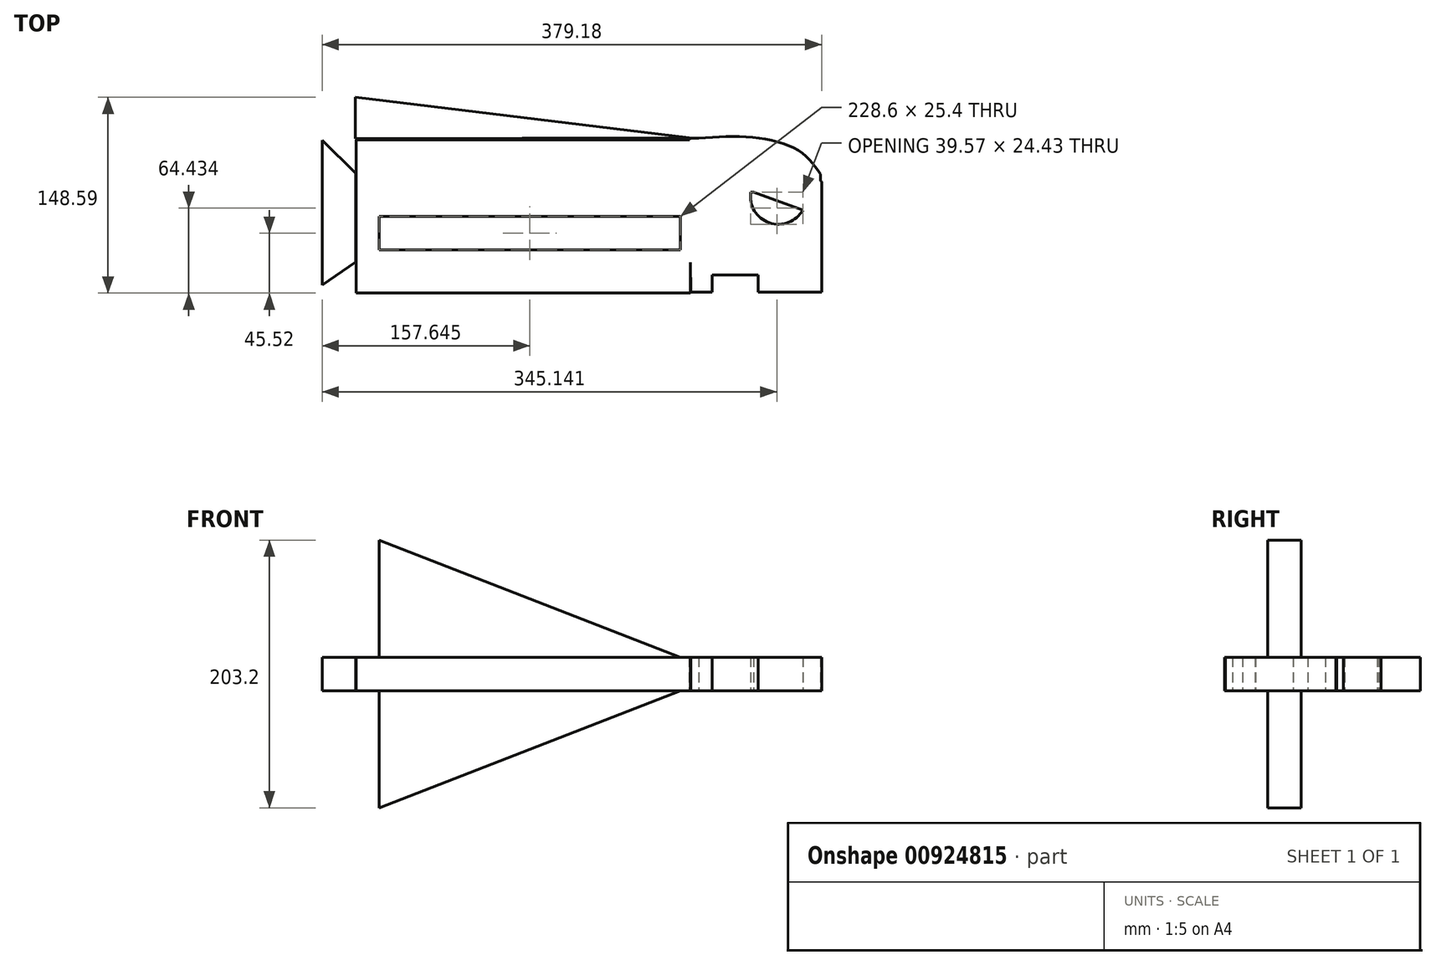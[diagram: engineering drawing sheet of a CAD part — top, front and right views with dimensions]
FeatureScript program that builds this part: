
annotation { "Feature Type Name" : "Feature", "Feature Type Description" : "" }
export const myFeature = defineFeature(function(context is Context, id is Id, definition is map)
    precondition{}
    {
        {
            var Q0;
            Q0=qCreatedBy(makeId("Top.planeOp"),FACE);
            var sketch = newSketch(context, id + "F0", { "sketchPlane" : qUnion([Q0])});
            skLineSegment(sketch, "E0.bottom", {"start": v(126.83, 58.22) * mm, "end": v(-126.83, 58.22) * mm});
            skLineSegment(sketch, "E0.top", {"start": v(126.83, -58.22) * mm, "end": v(-126.83, -58.22) * mm});
            skLineSegment(sketch, "E0.left", {"start": v(126.83, 58.22) * mm, "end": v(126.83, -58.22) * mm});
            skLineSegment(sketch, "E0.right", {"start": v(-126.83, 58.22) * mm, "end": v(-126.83, -58.22) * mm});
            skPoint(sketch, "E0.middle", {"position": v(0, 0) * mm});
            skSolve(sketch);
        }
        {
            var Q0;
            Q0=qCreatedBy(makeId("Top.planeOp"),FACE);
            var sketch = newSketch(context, id + "F1", { "sketchPlane" : qUnion([Q0])});
            skLineSegment(sketch, "E1", {"start": v(126.1, 59.34) * mm, "end": v(175.56, 59.34) * mm});
            skLineSegment(sketch, "E2", {"start": v(175.56, 59.34) * mm, "end": v(175.56, 41.8) * mm});
            skLineSegment(sketch, "E3", {"start": v(175.56, 41.8) * mm, "end": v(207.48, 41.8) * mm});
            skLineSegment(sketch, "E4", {"start": v(207.48, 41.8) * mm, "end": v(226.37, 26.23) * mm});
            skLineSegment(sketch, "E5", {"start": v(226.37, 26.23) * mm, "end": v(226.37, 0) * mm});
            skLineSegment(sketch, "E6", {"start": v(226.37, 0) * mm, "end": v(226.37, -17.54) * mm});
            skLineSegment(sketch, "E7", {"start": v(226.37, -17.54) * mm, "end": v(226.37, -44.52) * mm});
            skLineSegment(sketch, "E8", {"start": v(226.37, -44.52) * mm, "end": v(226.37, -57.55) * mm});
            skLineSegment(sketch, "E9", {"start": v(226.37, -57.55) * mm, "end": v(178.26, -57.55) * mm});
            skLineSegment(sketch, "E10", {"start": v(178.26, -57.55) * mm, "end": v(178.26, -44.52) * mm});
            skLineSegment(sketch, "E11", {"start": v(178.26, -44.52) * mm, "end": v(143.2, -44.52) * mm});
            skLineSegment(sketch, "E12", {"start": v(143.2, -44.52) * mm, "end": v(143.2, -57.55) * mm});
            skLineSegment(sketch, "E13", {"start": v(143.2, -57.55) * mm, "end": v(127, -57.55) * mm});
            skLineSegment(sketch, "E14", {"start": v(127, -57.55) * mm, "end": v(126.1, 59.34) * mm});
            skCircle(sketch, "E15", {"center": v(193.58, 15.27) * mm, "radius": 21.27 * mm});
            skPoint(sketch, "E15.first.point", {"position": v(180.96, 32.38) * mm});
            skPoint(sketch, "E15.second.point", {"position": v(208.39, 0) * mm});
            skPoint(sketch, "E15.third.point", {"position": v(196.52, -5.8) * mm});
            skFitSpline(sketch, "E16", {"points": [v(175.56, 59.34) * mm, v(199.5, 55.74) * mm, v(226.37, 26.23) * mm], "startDerivative": vector(56.16, 1.45) * mm, "endDerivative": vector(45.88, -64.93) * mm});
            skSolve(sketch);
        }
        {
            var Q0;
            Q0=qCreatedBy(makeId("Top.planeOp"),FACE);
            var sketch = newSketch(context, id + "F2", { "sketchPlane" : qUnion([Q0])});
            skLineSegment(sketch, "E17", {"start": v(127, 58.9) * mm, "end": v(140.94, 18.43) * mm});
            skLineSegment(sketch, "E18", {"start": v(140.94, 18.43) * mm, "end": v(174.66, 18.43) * mm});
            skLineSegment(sketch, "E19", {"start": v(174.66, 18.43) * mm, "end": v(225.47, 0) * mm});
            skLineSegment(sketch, "E20", {"start": v(225.47, 0) * mm, "end": v(225.47, 25.62) * mm});
            skLineSegment(sketch, "E21", {"start": v(225.47, 25.62) * mm, "end": v(225.47, 31.92) * mm});
            skFitSpline(sketch, "E22", {"points": [v(225.47, 31.92) * mm, v(210.18, 49) * mm, v(175.56, 59.8) * mm, v(127, 58.9) * mm], "startDerivative": vector(-47.19, 69.04) * mm, "endDerivative": vector(-126.46, -9.56) * mm});
            skSolve(sketch);
        }
        {
            var Q0;
            Q0=qCreatedBy(makeId("Top.planeOp"),FACE);
            var sketch = newSketch(context, id + "F3", { "sketchPlane" : qUnion([Q0])});
            skLineSegment(sketch, "E23", {"start": v(-127.47, 58.9) * mm, "end": v(-127.47, 90.37) * mm});
            skLineSegment(sketch, "E24", {"start": v(-127.47, 90.37) * mm, "end": v(125.66, 59.8) * mm});
            skLineSegment(sketch, "E25", {"start": v(125.66, 59.8) * mm, "end": v(-127.47, 58.9) * mm});
            skSolve(sketch);
        }
        {
            var Q0;
            Q0=qCreatedBy(makeId("Top.planeOp"),FACE);
            var sketch = newSketch(context, id + "F4", { "sketchPlane" : qUnion([Q0])});
            skLineSegment(sketch, "E26", {"start": v(-127.2, -34.56) * mm, "end": v(-152.8, -52.08) * mm});
            skLineSegment(sketch, "E27", {"start": v(-152.8, -52.08) * mm, "end": v(-152.8, 57.73) * mm});
            skLineSegment(sketch, "E28", {"start": v(-152.8, 57.73) * mm, "end": v(-127.2, 32.8) * mm});
            skLineSegment(sketch, "E29", {"start": v(-127.2, 32.8) * mm, "end": v(-127.2, -34.56) * mm});
            skSolve(sketch);
        }
        {
            var Q0;
            Q0=makeQuery(id+"F0.imprint","IMPRINT",FACE,{"disambiguationData":[TD([[makeQuery(id+"F0.imprint","IMPRINT",EDGE,{"derivedFrom":sQuery(id+"F0.wireOp",EDGE,"E0.bottom")}),1.0]])]});
            var Q1;
            Q1=makeQuery(id+"F3.imprint","IMPRINT",FACE,{"disambiguationData":[TD([[makeQuery(id+"F3.imprint","IMPRINT",EDGE,{"derivedFrom":sQuery(id+"F3.wireOp",EDGE,"E23")}),-1.0]])]});
            var Q2;
            Q2=makeQuery(id+"F4.imprint","IMPRINT",FACE,{"disambiguationData":[TD([[makeQuery(id+"F4.imprint","IMPRINT",EDGE,{"derivedFrom":sQuery(id+"F4.wireOp",EDGE,"E26")}),-1.0]])]});
            extrude(context, id + "F5", {"entities" : qUnion([Q0, Q1, Q2]), "depth" : 25.4 * mm, "offsetDistance" : 25.4 * mm});
        }
        {
            var Q0;
            Q0=makeQuery(id+"F2.imprint","IMPRINT",FACE,{"disambiguationData":[TD([[makeQuery(id+"F2.imprint","IMPRINT",EDGE,{"derivedFrom":sQuery(id+"F2.wireOp",EDGE,"E17")}),1.0]])]});
            extrude(context, id + "F6", {"entities" : qUnion([Q0]), "operationType" : NewBodyOperationType.ADD, "depth" : 25.4 * mm, "offsetDistance" : 25.4 * mm});
        }
        {
            var Q0;
            Q0=qCreatedBy(makeId("Front.planeOp"),FACE);
            var sketch = newSketch(context, id + "F7", { "sketchPlane" : qUnion([Q0])});
            skLineSegment(sketch, "E30", {"start": v(-109.47, 0) * mm, "end": v(-109.47, -88.9) * mm});
            skLineSegment(sketch, "E31", {"start": v(-109.47, -88.9) * mm, "end": v(119.13, 0) * mm});
            skLineSegment(sketch, "E32", {"start": v(119.13, 0) * mm, "end": v(119.13, 25.4) * mm});
            skLineSegment(sketch, "E33", {"start": v(119.13, 25.4) * mm, "end": v(-109.47, 114.3) * mm});
            skLineSegment(sketch, "E34", {"start": v(-109.47, 114.3) * mm, "end": v(-109.47, 25.4) * mm});
            skLineSegment(sketch, "E35", {"start": v(-109.47, 25.4) * mm, "end": v(-109.47, 0) * mm});
            skSolve(sketch);
        }
        {
            var Q0;
            Q0 = qSketchRegion(id + "F7", true);
            extrude(context, id + "F8", {"entities" : qUnion([Q0]), "operationType" : NewBodyOperationType.ADD, "depth" : 25.4 * mm, "offsetDistance" : 25.4 * mm});
        }
        {
            var Q0;
            Q0=makeQuery(id+"F1.imprint","IMPRINT",FACE,{"disambiguationData":[TD([[makeQuery(id+"F1.imprint","IMPRINT",EDGE,{"derivedFrom":sQuery(id+"F1.wireOp",EDGE,"E1")}),-1.0]])]});
            extrude(context, id + "F9", {"entities" : qUnion([Q0]), "operationType" : NewBodyOperationType.ADD, "depth" : 25.4 * mm, "offsetDistance" : 25.4 * mm});
        }
    });
